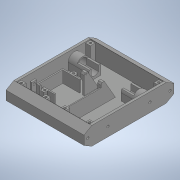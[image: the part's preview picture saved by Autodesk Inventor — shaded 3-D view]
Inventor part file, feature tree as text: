
AUTODESK INVENTOR PART (.ipt)
format: ipt  version: 2020 (Build 240168000, 168)  size: 630,272 bytes
history: native  units: in
note: dims shown in document units (in); Inventor stores cm internally (conversion verified against a paired STEP export)
features: extrude x18, sketch x18, projected_geometry x14, mirror x6, plane x1
ambient origin geometry x8: Origin, YZ Plane, XZ Plane, XY Plane, X Axis, Y Axis, Z Axis, Center Point
bodies: Solid1 (feature_tree)
feature tree (57):
  extrude  "Extrusion1"  Depth=5.9055in
  extrude  "Extrusion2"  TaperAngle=0.0deg  [1 undecoded]
  extrude  "Extrusion3"  Depth=1.063in
  extrude  "Extrusion4"  Depth=0.315in
  extrude  "Extrusion5"  TaperAngle=0.0deg  [1 undecoded]
  extrude  "Extrusion6"  Depth=0.5906in
  mirror  "Mirror1"
  extrude  "Extrusion7"  Depth=0.0787in
  mirror  "Mirror2"
  extrude  "Extrusion8"  Depth=0.6102in
  mirror  "Mirror3"
  plane  "Work Plane1"
  extrude  "Extrusion9"  Depth=0.7874in TaperAngle=0.0deg
  mirror  "Mirror4"
  extrude  "Extrusion10"  Depth=6.063in TaperAngle=0.0deg
  extrude  "Extrusion11"  Depth=0.1575in
  extrude  "Extrusion12"  TaperAngle=0.0deg  [1 undecoded]
  extrude  "Extrusion13"  Depth=0.2756in
  extrude  "Extrusion14"  Depth=0.4331in
  extrude  "Extrusion17"  Depth=2.7559in
  extrude  "Extrusion18"  Depth=0.0413in
  mirror  "Mirror6"
  extrude  "Extrusion19"  TaperAngle=0.0deg  [1 undecoded]
  mirror  "Mirror7"
  extrude  "Extrusion20"  Depth=0.0787in
  sketch  "Sketch1"  dims[d0=1.1811in d1=5.9055in]
  sketch  "Sketch2"  dims[d2=5.1181in d3=0.0in]
  projected_geometry  "Projected Loop1"
  sketch  "Sketch3"  dims[d4=0.1575in d5=1.063in]
  projected_geometry  "Projected Loop2"
  projected_geometry  "Projected Loop3"
  sketch  "Sketch4"  dims[d6=0.0in d8=0.315in]
  sketch  "Sketch5"  dims[d10=0.993in d11=0.0in]
  projected_geometry  "Projected Loop4"
  sketch  "Sketch6"  dims[d12=0.6496in d13=0.5906in]
  sketch  "Sketch7"  dims[d14=1.5748in d15=0.0787in]
  sketch  "Sketch9"  dims[d16=0.5512in d17=0.0in d18=0.6102in]
  sketch  "Sketch10"  dims[d19=0.4803in d20=0.7874in d21=0.0in]
  sketch  "Sketch12"  dims[d22=0.1654in d23=6.063in d24=0.0in]
  projected_geometry  "Projected Loop6"
  projected_geometry  "Projected Loop7"
  projected_geometry  "Projected Loop8"
  sketch  "Sketch13"  dims[d25=0.5114in d26=0.1575in]
  sketch  "Sketch14"  dims[d27=1.5748in d28=0.0in d29=0.0in]
  sketch  "Sketch15"  dims[d30=0.1575in d31=0.2756in]
  projected_geometry  "Projected Loop15"
  sketch  "Sketch16"  dims[d32=0.0in d33=0.4331in]
  projected_geometry  "Projected Loop19"
  projected_geometry  "Projected Loop20"
  projected_geometry  "Projected Loop21"
  projected_geometry  "Projected Loop22"
  projected_geometry  "Projected Loop23"
  projected_geometry  "Projected Loop24"
  sketch  "Sketch20"  dims[d34=0.0827in d38=2.7559in]
  sketch  "Sketch21"  dims[d40=0.0413in d41=0.0909in]
  sketch  "Sketch22"  dims[d42=0.2362in d43=0.0in]
  sketch  "Sketch23"  dims[d44=60.0deg d45=0.0787in d46=0.315in d48=0.993in d49=0.0in d53=0.2756in d54=0.0in d55=0.4724in d56=1.1811in d57=1.5748in d58=1.5748in d59=0.0787in d60=0.0787in d62=0.315in d63=0.7677in d64=0.0in d66=0.1476in d67=0.2756in d68=0.0in d69=0.7874in d70=0.2953in d71=0.1181in d72=0.0in d89=0.0157in d90=0.0157in d91=0.1476in d92=0.1476in d96=0.315in d97=0.1575in d98=0.1181in d99=0.0in d102=0.1772in d104=0.3346in d105=135.0deg d106=0.2362in d107=0.0in d108=0.0394in d109=0.0in d110=0.063in d111=0.0394in d112=0.0in]
note: 4 required parameter values undecoded (feature->parameter linkage not recoverable at this tier; creation-order binding heuristic only, values carry confidence <= 0.55)
